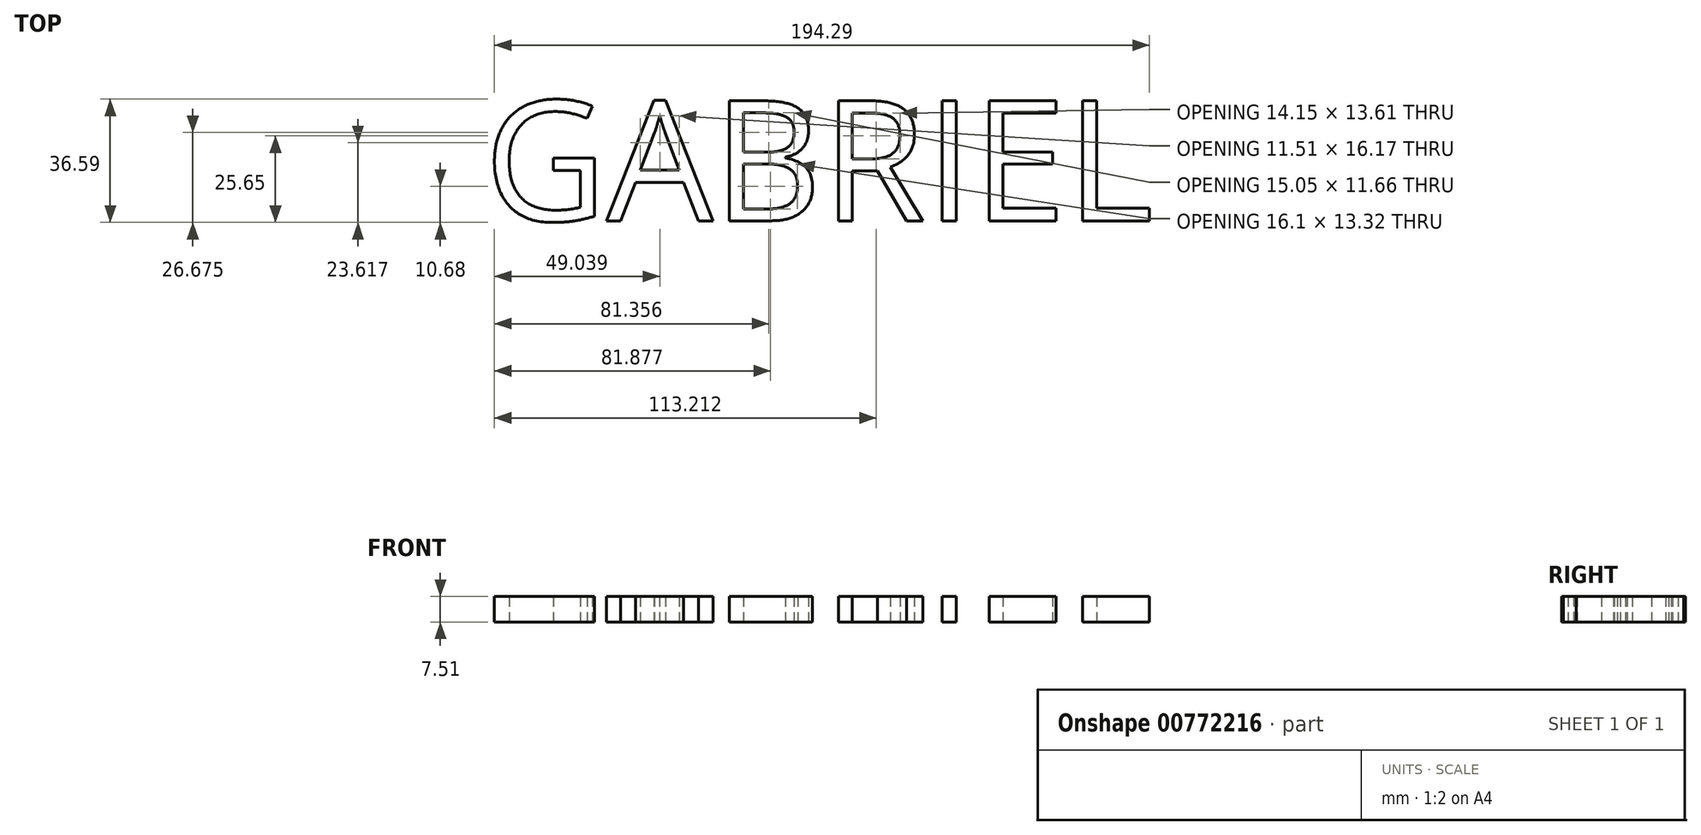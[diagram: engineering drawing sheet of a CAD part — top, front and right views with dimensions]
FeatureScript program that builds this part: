
annotation { "Feature Type Name" : "Feature", "Feature Type Description" : "" }
export const myFeature = defineFeature(function(context is Context, id is Id, definition is map)
    precondition{}
    {
        {
            var Q0;
            Q0=qCreatedBy(makeId("Top.planeOp"),FACE);
            var sketch = newSketch(context, id + "F0", { "sketchPlane" : qUnion([Q0])});
            skText(sketch, "E0", { "text": "GABRIEL", "fontName": "OpenSans-Regular.ttf"});
            const initialGuessF0  = {"E0": [0.03413, 0, 1, 0, 0.0359]};
            skSetInitialGuess(sketch, initialGuessF0);
            skSolve(sketch);
        }
        {
            var Q0;
            Q0=makeQuery(id+"F0.imprint","IMPRINT",FACE,{"disambiguationData":[TD([[makeQuery(id+"F0.imprint","IMPRINT",EDGE,{"derivedFrom":sQuery(id+"F0.wireOp",EDGE,"E0.sketch_text.stroke-33")}),-1.0]])]});
            var Q1;
            Q1=makeQuery(id+"F0.imprint","IMPRINT",FACE,{"disambiguationData":[TD([[makeQuery(id+"F0.imprint","IMPRINT",EDGE,{"derivedFrom":sQuery(id+"F0.wireOp",EDGE,"E0.sketch_text.stroke-20")}),-1.0]])]});
            var Q2;
            Q2=makeQuery(id+"F0.imprint","IMPRINT",FACE,{"disambiguationData":[TD([[makeQuery(id+"F0.imprint","IMPRINT",EDGE,{"derivedFrom":sQuery(id+"F0.wireOp",EDGE,"E0.sketch_text.stroke-0")}),-1.0]])]});
            var Q3;
            Q3=makeQuery(id+"F0.imprint","IMPRINT",FACE,{"disambiguationData":[TD([[makeQuery(id+"F0.imprint","IMPRINT",EDGE,{"derivedFrom":sQuery(id+"F0.wireOp",EDGE,"E0.sketch_text.stroke-58")}),-1.0]])]});
            var Q4;
            Q4=makeQuery(id+"F0.imprint","IMPRINT",FACE,{"disambiguationData":[TD([[makeQuery(id+"F0.imprint","IMPRINT",EDGE,{"derivedFrom":sQuery(id+"F0.wireOp",EDGE,"E0.sketch_text.stroke-76")}),-1.0]])]});
            var Q5;
            Q5=makeQuery(id+"F0.imprint","IMPRINT",FACE,{"disambiguationData":[TD([[makeQuery(id+"F0.imprint","IMPRINT",EDGE,{"derivedFrom":sQuery(id+"F0.wireOp",EDGE,"E0.sketch_text.stroke-80")}),-1.0]])]});
            var Q6;
            Q6=makeQuery(id+"F0.imprint","IMPRINT",FACE,{"disambiguationData":[TD([[makeQuery(id+"F0.imprint","IMPRINT",EDGE,{"derivedFrom":sQuery(id+"F0.wireOp",EDGE,"E0.sketch_text.stroke-92")}),-1.0]])]});
            var Q7;
            Q7 = qBodyType(qCreatedBy(id + "F0" ,EDGE), BodyType.WIRE);
            extrude(context, id + "F1", {"entities" : qUnion([Q0, Q1, Q2, Q3, Q4, Q5, Q6]), "surfaceEntities" : qUnion([Q7]), "depth" : 7.5 * mm, "offsetDistance" : 25.4 * mm});
        }
    });
